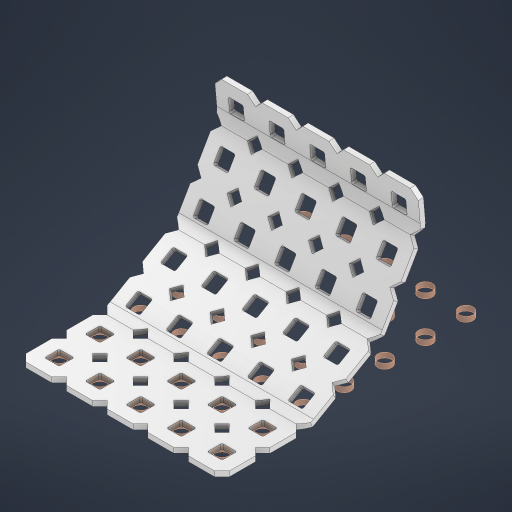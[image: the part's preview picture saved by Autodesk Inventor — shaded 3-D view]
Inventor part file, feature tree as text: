
AUTODESK INVENTOR PART (.ipt)
format: ipt  version: 2024 (Build 280153000, 153)  size: 1,040,896 bytes
history: native  units: in
note: dims shown in document units (in); Inventor stores cm internally (conversion verified against a paired STEP export)
features: other x39, extrude x34, sketch x3, pattern_linear x1
ambient origin geometry x8: Origin, YZ Plane, XZ Plane, XY Plane, X Axis, Y Axis, Z Axis, Center Point
bodies: Solid1 (feature_tree), Body (feature_tree)
feature tree (77):
  pattern_linear  "Rectangular Pattern1"  Spacing1=0.09in  [1 undecoded]
  other  "Bend Part1"
  other  "Bend Part2"
  other  "Bend Part3"
  other  "Srf1"
  other  "Srf126"
  other  "Srf127"
  other  "Srf128"
  other  "Srf129"
  other  "Srf130"
  other  "Srf131"
  other  "Srf268"
  other  "Srf269"
  other  "Srf270"
  other  "Srf271"
  other  "Srf272"
  other  "Srf273"
  other  "Srf274"
  other  "Srf293"
  other  "Srf294"
  other  "Srf295"
  other  "Srf296"
  other  "Srf297"
  other  "Srf298"
  other  "Srf299"
  other  "Srf318"
  other  "Srf319"
  other  "Srf320"
  other  "Srf321"
  other  "Srf322"
  other  "Srf323"
  other  "Srf324"
  other  "Srf343"
  other  "Srf344"
  other  "Srf345"
  other  "Srf346"
  other  "Srf347"
  other  "Srf348"
  other  "Srf349"
  sketch  "Sketch3"  dims[d1=0.5in]
  sketch  "Sketch4"  dims[d2=0.182in]
  sketch  "Sketch5"  dims[d3=0.09in d4=0.09in d5=0.09in d6=0.09in d7=0.09in d8=0.09in d9=0.09in d10=0.09in d11=0.02in d13=0.0in d14=0.172in d15=0.0625in d16=0.0in d19=0.5in d22=0.5in d23=0.25in d24=30.0deg d25=0.25in d26=30.0deg d27=0.25in d28=0.2405in]
  other  "Circle"
  extrude  "ExtrusionSrf126"  Depth=0.25in
  extrude  "ExtrusionSrf127"  Depth=0.25in
  extrude  "ExtrusionSrf128"  Depth=0.25in
  extrude  "ExtrusionSrf129"  Depth=0.25in
  extrude  "ExtrusionSrf130"  Depth=0.25in
  extrude  "ExtrusionSrf131"  Depth=0.25in
  extrude  "ExtrusionSrf268"  Depth=0.25in
  extrude  "ExtrusionSrf269"  TaperAngle=0.0deg  [1 undecoded]
  extrude  "ExtrusionSrf270"  Depth=0.25in
  extrude  "ExtrusionSrf271"  Depth=0.0625in TaperAngle=0.0deg
  extrude  "ExtrusionSrf272"  Depth=0.25in
  extrude  "ExtrusionSrf273"  Depth=0.25in
  extrude  "ExtrusionSrf274"  Depth=0.25in TaperAngle=30.0deg
  extrude  "ExtrusionSrf293"  Depth=0.25in TaperAngle=30.0deg
  extrude  "ExtrusionSrf294"  Depth=0.25in
  extrude  "ExtrusionSrf295"  [1 undecoded]
  extrude  "ExtrusionSrf296"  [1 undecoded]
  extrude  "ExtrusionSrf297"  [1 undecoded]
  extrude  "ExtrusionSrf298"  [1 undecoded]
  extrude  "ExtrusionSrf299"  [1 undecoded]
  extrude  "ExtrusionSrf318"  [1 undecoded]
  extrude  "ExtrusionSrf319"  [1 undecoded]
  extrude  "ExtrusionSrf320"  [1 undecoded]
  extrude  "ExtrusionSrf321"  [1 undecoded]
  extrude  "ExtrusionSrf322"  [1 undecoded]
  extrude  "ExtrusionSrf323"  [1 undecoded]
  extrude  "ExtrusionSrf324"  [1 undecoded]
  extrude  "ExtrusionSrf343"  [1 undecoded]
  extrude  "ExtrusionSrf344"  [1 undecoded]
  extrude  "ExtrusionSrf345"  [1 undecoded]
  extrude  "ExtrusionSrf346"  [1 undecoded]
  extrude  "ExtrusionSrf347"  [1 undecoded]
  extrude  "ExtrusionSrf348"  [1 undecoded]
  extrude  "ExtrusionSrf349"  [1 undecoded]
note: 21 required parameter values undecoded (feature->parameter linkage not recoverable at this tier; creation-order binding heuristic only, values carry confidence <= 0.55)
